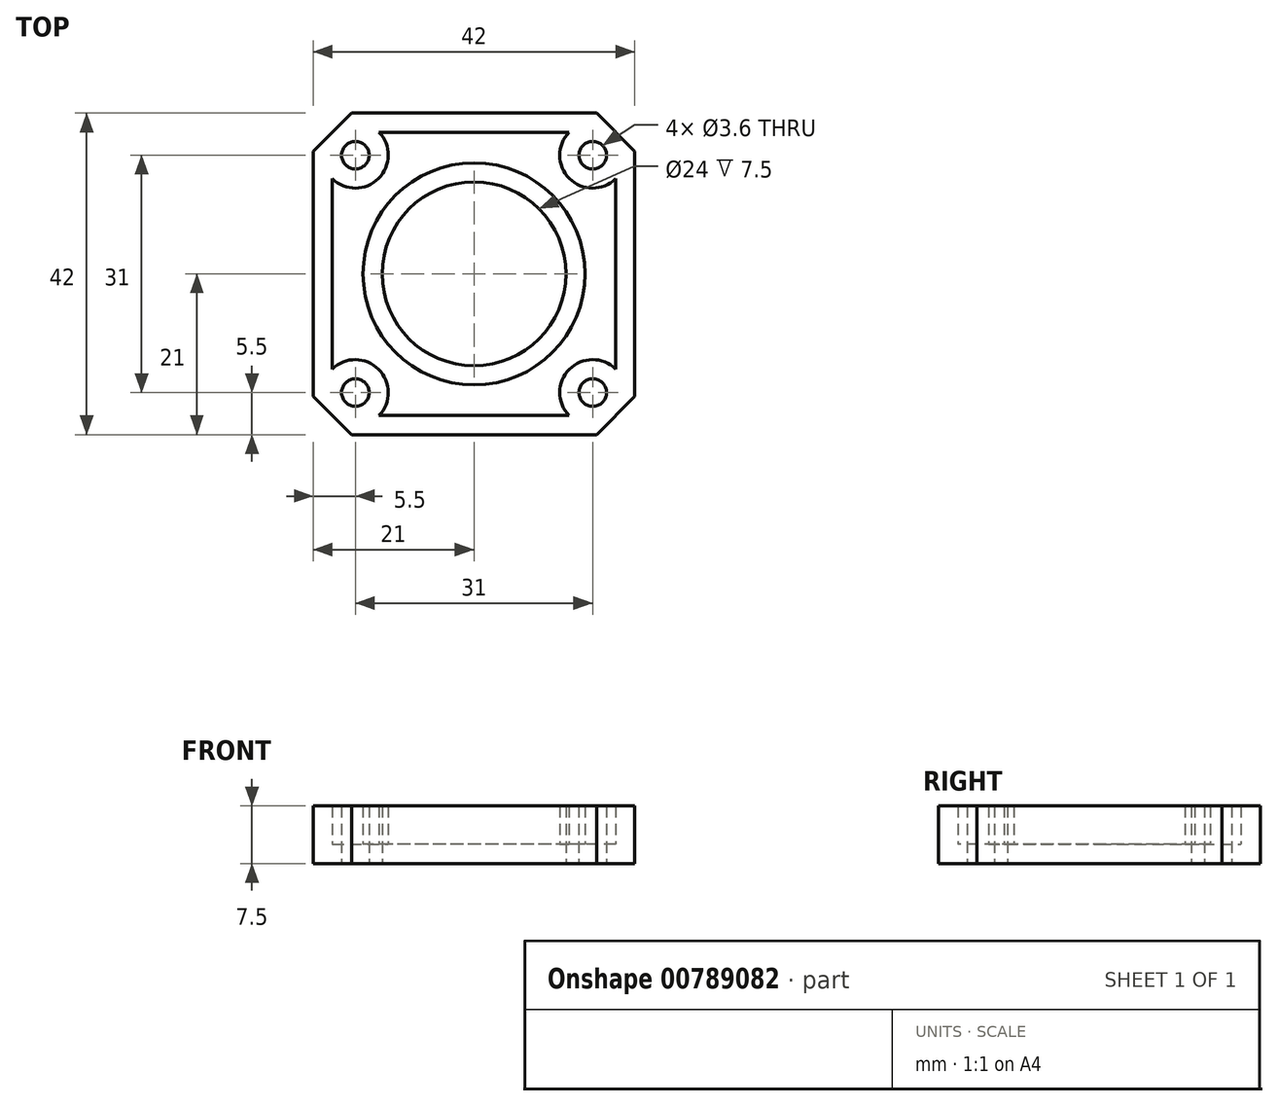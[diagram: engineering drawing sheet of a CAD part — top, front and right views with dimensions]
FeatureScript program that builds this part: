
annotation { "Feature Type Name" : "Feature", "Feature Type Description" : "" }
export const myFeature = defineFeature(function(context is Context, id is Id, definition is map)
    precondition{}
    {
        {
            var Q0;
            Q0=qCreatedBy(makeId("Top.planeOp"),FACE);
            var sketch = newSketch(context, id + "F0", { "sketchPlane" : qUnion([Q0])});
            skLineSegment(sketch, "E0.bottom", {"start": v(21, 21) * mm, "end": v(-21, 21) * mm});
            skLineSegment(sketch, "E0.top", {"start": v(21, -21) * mm, "end": v(-21, -21) * mm});
            skLineSegment(sketch, "E0.left", {"start": v(21, 21) * mm, "end": v(21, -21) * mm});
            skLineSegment(sketch, "E0.right", {"start": v(-21, 21) * mm, "end": v(-21, -21) * mm});
            skPoint(sketch, "E0.middle", {"position": v(0, 0) * mm});
            skCircle(sketch, "E1", {"center": v(0, 0) * mm, "radius": 12 * mm});
            skLineSegment(sketch, "E2.bottom", {"start": v(15.5, 15.5) * mm, "end": v(-15.5, 15.5) * mm, "construction": true});
            skLineSegment(sketch, "E2.top", {"start": v(15.5, -15.5) * mm, "end": v(-15.5, -15.5) * mm, "construction": true});
            skLineSegment(sketch, "E2.left", {"start": v(15.5, 15.5) * mm, "end": v(15.5, -15.5) * mm, "construction": true});
            skLineSegment(sketch, "E2.right", {"start": v(-15.5, 15.5) * mm, "end": v(-15.5, -15.5) * mm, "construction": true});
            skCircle(sketch, "E3", {"center": v(-15.5, -15.5) * mm, "radius": 1.8 * mm});
            skCircle(sketch, "E4.0.1.0", {"center": v(-15.5, 15.5) * mm, "radius": 1.8 * mm});
            skCircle(sketch, "E4.1.0.0", {"center": v(15.5, -15.5) * mm, "radius": 1.8 * mm});
            skCircle(sketch, "E4.1.1.0", {"center": v(15.5, 15.5) * mm, "radius": 1.8 * mm});
            skLineSegment(sketch, "E4.direction1", {"start": v(-15.5, -15.5) * mm, "end": v(15.5, -15.5) * mm, "construction": true});
            skLineSegment(sketch, "E4.direction2", {"start": v(-15.5, -15.5) * mm, "end": v(-15.5, 15.5) * mm, "construction": true});
            skSolve(sketch);
        }
        {
            var Q0;
            Q0 = qSketchRegion(id + "F0", true);
            extrude(context, id + "F1", {"entities" : qUnion([Q0]), "depth" : 7.5 * mm, "offsetDistance" : 25 * mm});
        }
        {
            var Q0;
            Q0=makeQuery(id+"F1.opExtrude","SWEPT_EDGE",EDGE,{"disambiguationData":[OSD([sQuery(id+"F0.wireOp",EDGE,"E0.top"),sQuery(id+"F0.wireOp",EDGE,"E0.left")])]});
            var Q1;
            Q1=makeQuery(id+"F1.opExtrude","SWEPT_EDGE",EDGE,{"disambiguationData":[OSD([sQuery(id+"F0.wireOp",EDGE,"E0.bottom"),sQuery(id+"F0.wireOp",EDGE,"E0.left")])]});
            var Q2;
            Q2=makeQuery(id+"F1.opExtrude","SWEPT_EDGE",EDGE,{"disambiguationData":[OSD([sQuery(id+"F0.wireOp",EDGE,"E0.top"),sQuery(id+"F0.wireOp",EDGE,"E0.right")])]});
            var Q3;
            Q3=makeQuery(id+"F1.opExtrude","SWEPT_EDGE",EDGE,{"disambiguationData":[OSD([sQuery(id+"F0.wireOp",EDGE,"E0.bottom"),sQuery(id+"F0.wireOp",EDGE,"E0.right")])]});
            chamfer(context, id + "F2", {"entities" : qUnion([Q0, Q1, Q2, Q3]), "width" : 5 * mm, "tangentPropagation" : true});
        }
        {
            var Q0;
            Q0=makeQuery(id+"F1.opExtrude","CAP_FACE",FACE,{"disambiguationData":[OSD([sQuery(id+"F0.wireOp",EDGE,"E0.bottom"),sQuery(id+"F0.wireOp",EDGE,"E0.top"),sQuery(id+"F0.wireOp",EDGE,"E0.left"),sQuery(id+"F0.wireOp",EDGE,"E0.right"),sQuery(id+"F0.wireOp",EDGE,"E1"),sQuery(id+"F0.wireOp",EDGE,"E3"),sQuery(id+"F0.wireOp",EDGE,"E4.0.1.0"),sQuery(id+"F0.wireOp",EDGE,"E4.1.0.0"),sQuery(id+"F0.wireOp",EDGE,"E4.1.1.0")])],"isStart":false});
            shell(context, id + "F3", {"entities" : qUnion([Q0]), "thickness" : 2.5 * mm});
        }
    });
